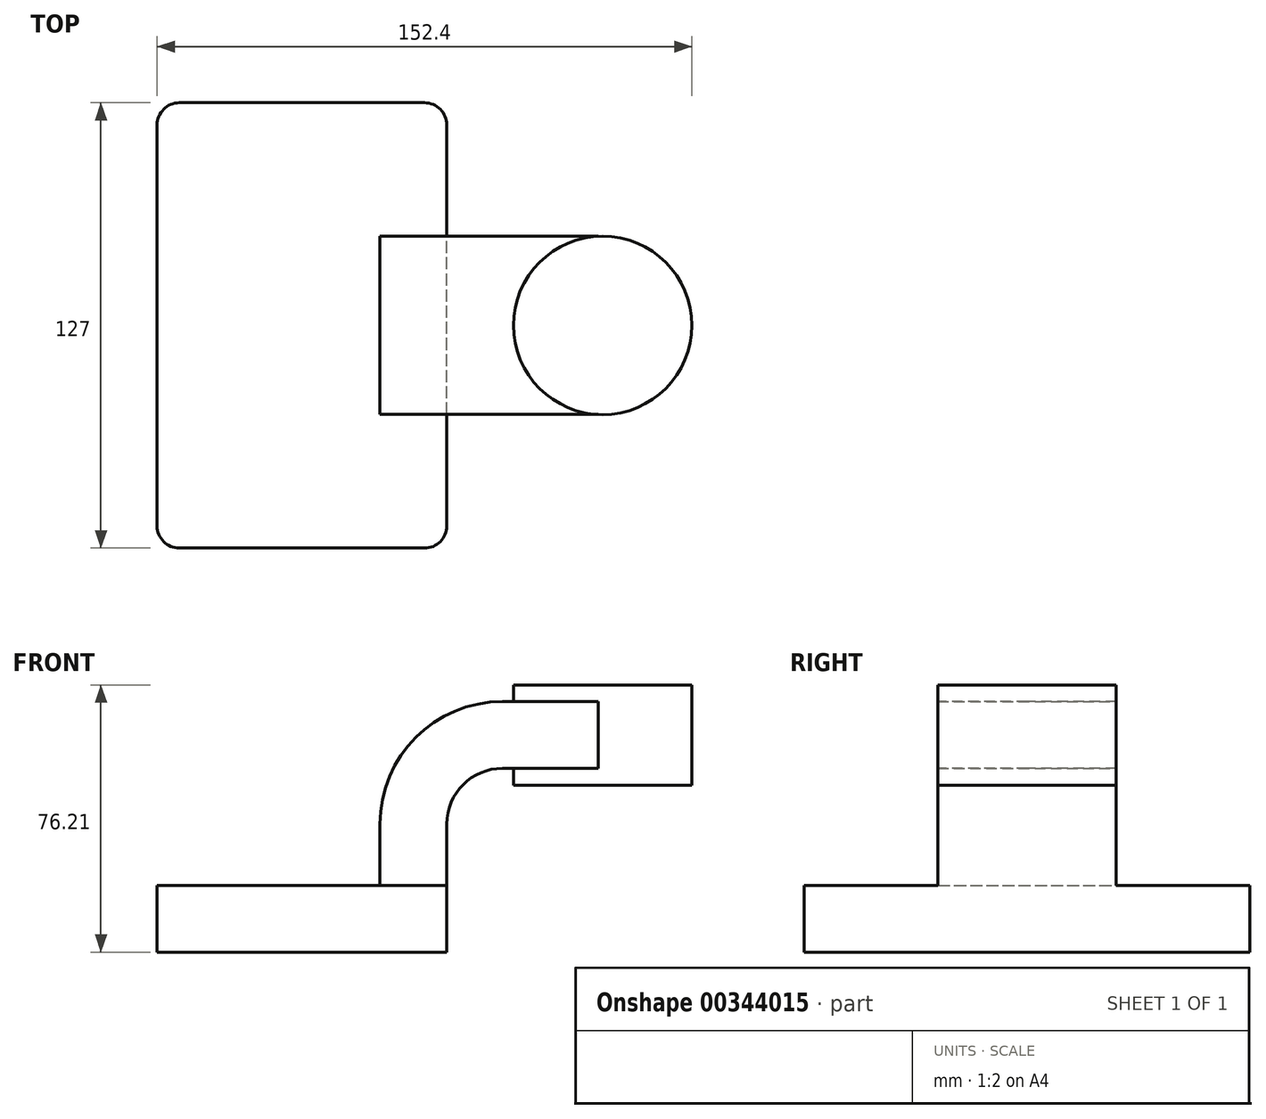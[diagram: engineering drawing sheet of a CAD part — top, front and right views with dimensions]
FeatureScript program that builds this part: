
annotation { "Feature Type Name" : "Feature", "Feature Type Description" : "" }
export const myFeature = defineFeature(function(context is Context, id is Id, definition is map)
    precondition{}
    {
        {
            var Q0;
            Q0=qCreatedBy(makeId("Front.planeOp"),FACE);
            var sketch = newSketch(context, id + "F0", { "sketchPlane" : qUnion([Q0])});
            skLineSegment(sketch, "E0.bottom", {"start": v(41.27, 9.53) * mm, "end": v(-41.28, 9.53) * mm});
            skLineSegment(sketch, "E0.top", {"start": v(41.28, -9.52) * mm, "end": v(-41.27, -9.52) * mm});
            skLineSegment(sketch, "E0.left", {"start": v(41.28, 9.53) * mm, "end": v(41.28, -9.52) * mm});
            skLineSegment(sketch, "E0.right", {"start": v(-41.28, 9.53) * mm, "end": v(-41.27, -9.52) * mm});
            skPoint(sketch, "E0.middle", {"position": v(0, 0) * mm});
            skLineSegment(sketch, "E1.bottom", {"start": v(60.33, 38.1) * mm, "end": v(111.13, 38.1) * mm});
            skLineSegment(sketch, "E1.top", {"start": v(60.33, 66.68) * mm, "end": v(111.12, 66.68) * mm});
            skLineSegment(sketch, "E1.left", {"start": v(60.33, 38.1) * mm, "end": v(60.32, 66.67) * mm});
            skLineSegment(sketch, "E1.right", {"start": v(111.12, 38.1) * mm, "end": v(111.12, 66.68) * mm});
            skPoint(sketch, "E1.middle", {"position": v(85.72, 52.39) * mm});
            skLineSegment(sketch, "E2", {"start": v(41.27, 9.53) * mm, "end": v(41.27, 27) * mm});
            skArc(sketch, "E3", {"start": v(41.27, 27) * mm, "mid": v(45.92, 38.23) * mm, "end": v(57.15, 42.88) * mm});
            skLineSegment(sketch, "E4", {"start": v(57.15, 42.88) * mm, "end": v(85.7, 42.88) * mm});
            skLineSegment(sketch, "E5.0", {"start": v(57.15, 61.93) * mm, "end": v(96.03, 61.93) * mm});
            skArc(sketch, "E5.1", {"start": v(22.23, 27) * mm, "mid": v(32.45, 51.7) * mm, "end": v(57.15, 61.93) * mm});
            skLineSegment(sketch, "E5.2", {"start": v(22.22, 9.53) * mm, "end": v(22.22, 27) * mm});
            skLineSegment(sketch, "E6", {"start": v(85.7, 38.1) * mm, "end": v(85.7, 66.68) * mm});
            skPoint(sketch, "E6.startSnap0", {"position": v(85.73, 38.1) * mm});
            skFitSpline(sketch, "E7", {"points": [v(-41.28, 9.53) * mm, v(57.15, 61.93) * mm], "startDerivative": vector(-1.56, 91.1) * mm, "endDerivative": vector(138.27, -29.03) * mm});
            skSolve(sketch);
        }
        {
            var Q0;
            Q0=makeQuery(id+"F0.imprint","IMPRINT",FACE,{"disambiguationData":[TD([[makeQuery(id+"F0.imprint","IMPRINT",EDGE,{"derivedFrom":sQuery(id+"F0.wireOp",EDGE,"E0.top")}),-1.0]])]});
            extrude(context, id + "F1", {"entities" : qUnion([Q0]), "endBound" : BoundingType.SYMMETRIC, "depth" : 127 * mm});
        }
        {
            var Q0;
            {var subQ1=sQuery(id+"F0.wireOp",EDGE,"E2");Q0=makeQuery(id+"F0.imprint","IMPRINT",FACE,{"disambiguationData":[TD([[makeQuery(id+"F0.imprint","IMPRINT",EDGE,{"derivedFrom":subQ1}),1.0]])]});}
            var Q1;
            {var subQ0=sQuery(id+"F0.wireOp",EDGE,"E4");var subQ1=sQuery(id+"F0.wireOp",EDGE,"E1.left");var subQ2=makeQuery(id+"F0.imprint","INTERSECT",VERTEX,{"derivedFrom":[subQ1,subQ0]});Q1=makeQuery(id+"F0.imprint","IMPRINT",FACE,{"disambiguationData":[TD([[makeQuery(id+"F0.imprint","IMPRINT",EDGE,{"disambiguationData":[TD([[subQ2,-1.0]])],"derivedFrom":subQ1}),-1.0]])]});}
            extrude(context, id + "F2", {"entities" : qUnion([Q0, Q1]), "operationType" : NewBodyOperationType.ADD, "endBound" : BoundingType.SYMMETRIC, "depth" : 50.8 * mm});
        }
        {
            var Q0;
            Q0=makeQuery(id+"F0.imprint","IMPRINT",FACE,{"disambiguationData":[TD([[makeQuery(id+"F0.imprint","IMPRINT",EDGE,{"derivedFrom":sQuery(id+"F0.wireOp",EDGE,"E5.1")}),1.0]])]});
            extrude(context, id + "F3", {"entities" : qUnion([Q0]), "operationType" : NewBodyOperationType.ADD, "endBound" : BoundingType.SYMMETRIC, "depth" : 15.88 * mm});
        }
        {
            var Q0;
            {var subQ0=sQuery(id+"F0.wireOp",EDGE,"E1.right");Q0=makeQuery(id+"F0.imprint","IMPRINT",FACE,{"disambiguationData":[TD([[makeQuery(id+"F0.imprint","IMPRINT",EDGE,{"derivedFrom":subQ0}),1.0]])]});}
            var Q1;
            Q1=sQuery(id+"F0.wireOp",EDGE,"E6");
            revolve(context, id + "F4", {"operationType" : NewBodyOperationType.ADD, "entities" : qUnion([Q0]), "axis" : qUnion([Q1]), "revolveType" : RevolveType.FULL});
        }
        {
            var Q0;
            Q0=makeQuery(id+"F1.opExtrude","CAP_EDGE",EDGE,{"disambiguationData":[OSD([sQuery(id+"F0.wireOp",EDGE,"E0.left")])],"isStart":false});
            var Q1;
            Q1=makeQuery(id+"F1.opExtrude","CAP_EDGE",EDGE,{"disambiguationData":[OSD([sQuery(id+"F0.wireOp",EDGE,"E0.right")])],"isStart":false});
            var Q2;
            Q2=makeQuery(id+"F1.opExtrude","CAP_EDGE",EDGE,{"disambiguationData":[OSD([sQuery(id+"F0.wireOp",EDGE,"E0.left")])],"isStart":true});
            var Q3;
            Q3=makeQuery(id+"F1.opExtrude","CAP_EDGE",EDGE,{"disambiguationData":[OSD([sQuery(id+"F0.wireOp",EDGE,"E0.right")])],"isStart":true});
            fillet(context, id + "F5", {"entities" : qUnion([Q0, Q1, Q2, Q3]), "radius" : 6.35 * mm, "tangentPropagation" : true, "allowEdgeOverflow" : false});
        }
    });
